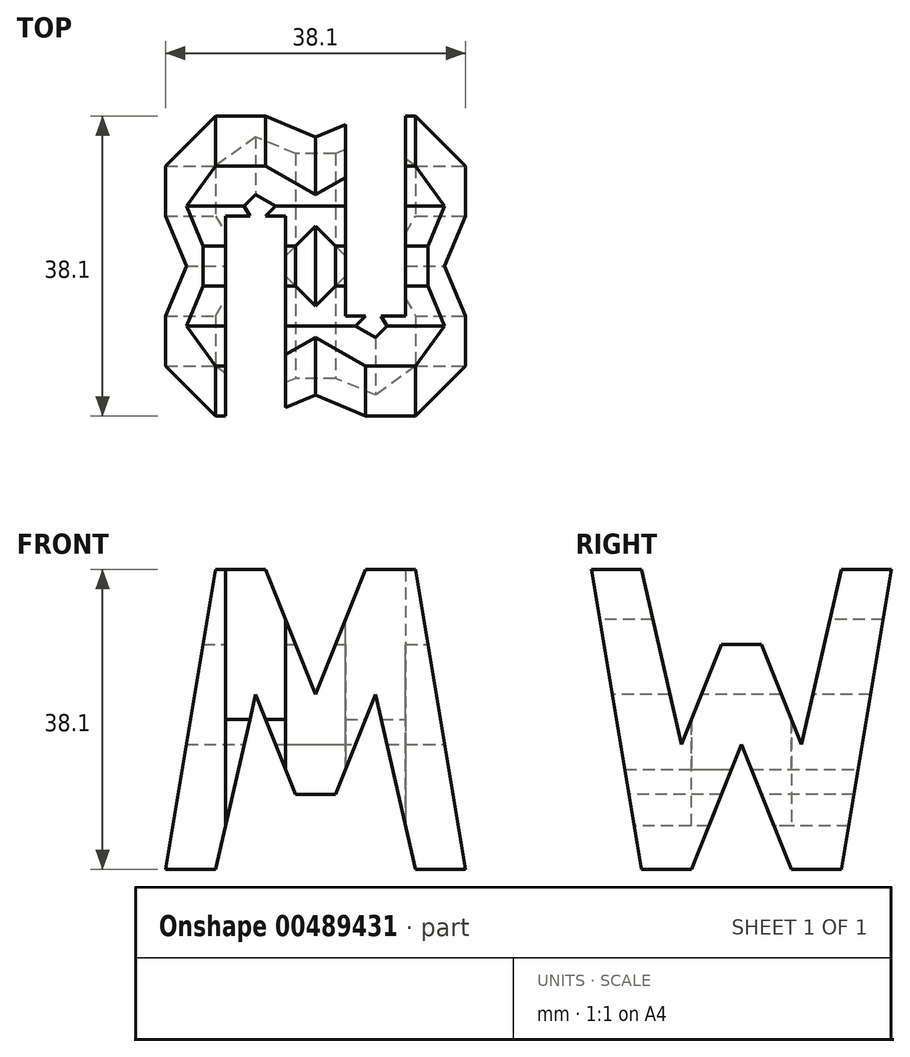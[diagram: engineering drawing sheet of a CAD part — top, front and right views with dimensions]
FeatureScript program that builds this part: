
annotation { "Feature Type Name" : "Feature", "Feature Type Description" : "" }
export const myFeature = defineFeature(function(context is Context, id is Id, definition is map)
    precondition{}
    {
        {
            var Q0;
            Q0=qCreatedBy(makeId("Front.planeOp"),FACE);
            var sketch = newSketch(context, id + "F0", { "sketchPlane" : qUnion([Q0])});
            skLineSegment(sketch, "E0.bottom", {"start": v(0, 0) * mm, "end": v(38.1, 0) * mm});
            skLineSegment(sketch, "E0.top", {"start": v(0, 38.1) * mm, "end": v(38.1, 38.1) * mm});
            skLineSegment(sketch, "E0.left", {"start": v(0, 0) * mm, "end": v(0, 38.1) * mm});
            skLineSegment(sketch, "E0.right", {"start": v(38.1, 0) * mm, "end": v(38.1, 38.1) * mm});
            skSolve(sketch);
        }
        {
            var Q0;
            Q0 = qSketchRegion(id + "F0", true);
            extrude(context, id + "F1", {"entities" : qUnion([Q0]), "depth" : 38.1 * mm, "offsetDistance" : 25.4 * mm});
        }
        {
            var Q0;
            Q0=qCreatedBy(makeId("Front.planeOp"),FACE);
            cPlane(context, id + "F2", {"entities" : qUnion([Q0]), "cplaneType" : CPlaneType.OFFSET, "offset" : 38.1 * mm, "width" : 152.4 * mm, "height" : 152.4 * mm});
        }
        {
            var Q0;
            Q0=qCreatedBy(makeId("Right.planeOp"),FACE);
            cPlane(context, id + "F3", {"entities" : qUnion([Q0]), "cplaneType" : CPlaneType.OFFSET, "offset" : 38.1 * mm, "width" : 152.4 * mm, "height" : 152.4 * mm});
        }
        {
            var Q0;
            Q0=qCreatedBy(id+"F3.planeOp",FACE);
            var sketch = newSketch(context, id + "F4", { "sketchPlane" : qUnion([Q0])});
            skLineSegment(sketch, "E1.bottom", {"start": v(0, 0) * mm, "end": v(-38.1, 0) * mm});
            skLineSegment(sketch, "E1.top", {"start": v(0, 38.1) * mm, "end": v(-38.1, 38.1) * mm});
            skLineSegment(sketch, "E1.left", {"start": v(0, 0) * mm, "end": v(0, 38.1) * mm});
            skLineSegment(sketch, "E1.right", {"start": v(-38.1, 0) * mm, "end": v(-38.1, 38.1) * mm});
            skLineSegment(sketch, "E2", {"start": v(0, 38.1) * mm, "end": v(-6.35, 0) * mm});
            skLineSegment(sketch, "E3", {"start": v(-38.1, 38.1) * mm, "end": v(-31.75, 0) * mm});
            skLineSegment(sketch, "E4", {"start": v(-25.4, 0) * mm, "end": v(-19.05, 15.88) * mm});
            skLineSegment(sketch, "E5", {"start": v(-12.7, 0) * mm, "end": v(-19.05, 15.88) * mm});
            skLineSegment(sketch, "E6", {"start": v(-31.75, 38.1) * mm, "end": v(-26.67, 15.88) * mm});
            skLineSegment(sketch, "E7", {"start": v(-6.35, 38.1) * mm, "end": v(-11.43, 15.88) * mm});
            skLineSegment(sketch, "E8", {"start": v(-11.43, 15.88) * mm, "end": v(-16.5, 28.58) * mm});
            skLineSegment(sketch, "E9", {"start": v(-26.67, 15.88) * mm, "end": v(-21.59, 28.58) * mm});
            skLineSegment(sketch, "E10", {"start": v(-16.5, 28.58) * mm, "end": v(-21.59, 28.58) * mm});
            skLineSegment(sketch, "E11", {"start": v(-38.1, 0) * mm, "end": v(0, 0) * mm});
            skSolve(sketch);
        }
        {
            var Q0;
            {var subQ1=sQuery(id+"F4.wireOp",EDGE,"E6");Q0=makeQuery(id+"F4.imprint","IMPRINT",FACE,{"disambiguationData":[TD([[makeQuery(id+"F4.imprint","IMPRINT",EDGE,{"derivedFrom":subQ1}),1.0]])]});}
            var Q1;
            {var subQ0=sQuery(id+"F4.wireOp",EDGE,"E1.right");Q1=makeQuery(id+"F4.imprint","IMPRINT",FACE,{"disambiguationData":[TD([[makeQuery(id+"F4.imprint","IMPRINT",EDGE,{"derivedFrom":subQ0}),-1.0]])]});}
            var Q2;
            {var subQ0=sQuery(id+"F4.wireOp",EDGE,"E4");Q2=makeQuery(id+"F4.imprint","IMPRINT",FACE,{"disambiguationData":[TD([[makeQuery(id+"F4.imprint","IMPRINT",EDGE,{"derivedFrom":subQ0}),-1.0]])]});}
            var Q3;
            {var subQ0=sQuery(id+"F4.wireOp",EDGE,"E1.left");Q3=makeQuery(id+"F4.imprint","IMPRINT",FACE,{"disambiguationData":[TD([[makeQuery(id+"F4.imprint","IMPRINT",EDGE,{"derivedFrom":subQ0}),1.0]])]});}
            extrude(context, id + "F5", {"entities" : qUnion([Q0, Q1, Q2, Q3]), "operationType" : NewBodyOperationType.REMOVE, "oppositeDirection" : true, "depth" : 38.1 * mm, "offsetDistance" : 25.4 * mm});
        }
        {
            var Q0;
            Q0=qCreatedBy(id+"F2.planeOp",FACE);
            var sketch = newSketch(context, id + "F6", { "sketchPlane" : qUnion([Q0])});
            skLineSegment(sketch, "E12", {"start": v(0, 38.1) * mm, "end": v(0, 0) * mm});
            skLineSegment(sketch, "E13", {"start": v(38.1, 0) * mm, "end": v(0, 0) * mm});
            skLineSegment(sketch, "E14", {"start": v(38.1, 0) * mm, "end": v(38.1, 38.1) * mm});
            skLineSegment(sketch, "E15", {"start": v(38.1, 38.1) * mm, "end": v(0, 38.1) * mm});
            skLineSegment(sketch, "E16", {"start": v(0, 0) * mm, "end": v(6.35, 38.1) * mm});
            skLineSegment(sketch, "E17", {"start": v(12.7, 38.1) * mm, "end": v(19.05, 22.23) * mm});
            skLineSegment(sketch, "E18", {"start": v(19.05, 22.23) * mm, "end": v(25.4, 38.1) * mm});
            skLineSegment(sketch, "E19", {"start": v(31.75, 38.1) * mm, "end": v(38.1, 0) * mm});
            skLineSegment(sketch, "E20", {"start": v(31.75, 0) * mm, "end": v(26.67, 22.23) * mm});
            skLineSegment(sketch, "E21", {"start": v(26.67, 22.22) * mm, "end": v(21.59, 9.53) * mm});
            skLineSegment(sketch, "E22", {"start": v(21.59, 9.53) * mm, "end": v(16.5, 9.53) * mm});
            skLineSegment(sketch, "E23", {"start": v(16.5, 9.53) * mm, "end": v(11.43, 22.23) * mm});
            skLineSegment(sketch, "E24", {"start": v(11.43, 22.23) * mm, "end": v(6.35, 0) * mm});
            skSolve(sketch);
        }
        {
            var Q0;
            {var subQ0=sQuery(id+"F6.wireOp",EDGE,"E12");Q0=makeQuery(id+"F6.imprint","IMPRINT",FACE,{"disambiguationData":[TD([[makeQuery(id+"F6.imprint","IMPRINT",EDGE,{"derivedFrom":subQ0}),1.0]])]});}
            var Q1;
            {var subQ0=sQuery(id+"F6.wireOp",EDGE,"E17");Q1=makeQuery(id+"F6.imprint","IMPRINT",FACE,{"disambiguationData":[TD([[makeQuery(id+"F6.imprint","IMPRINT",EDGE,{"derivedFrom":subQ0}),1.0]])]});}
            var Q2;
            {var subQ0=sQuery(id+"F6.wireOp",EDGE,"E14");Q2=makeQuery(id+"F6.imprint","IMPRINT",FACE,{"disambiguationData":[TD([[makeQuery(id+"F6.imprint","IMPRINT",EDGE,{"derivedFrom":subQ0}),1.0]])]});}
            var Q3;
            {var subQ0=sQuery(id+"F6.wireOp",EDGE,"E20");Q3=makeQuery(id+"F6.imprint","IMPRINT",FACE,{"disambiguationData":[TD([[makeQuery(id+"F6.imprint","IMPRINT",EDGE,{"derivedFrom":subQ0}),1.0]])]});}
            extrude(context, id + "F7", {"entities" : qUnion([Q0, Q1, Q2, Q3]), "operationType" : NewBodyOperationType.REMOVE, "oppositeDirection" : true, "depth" : 38.1 * mm, "offsetDistance" : 25.4 * mm});
        }
        {
            var Q0;
            Q0=qCreatedBy(makeId("Top.planeOp"),FACE);
            var sketch = newSketch(context, id + "F8", { "sketchPlane" : qUnion([Q0])});
            skLineSegment(sketch, "E25", {"start": v(7.62, -38.1) * mm, "end": v(7.62, -12.7) * mm});
            skLineSegment(sketch, "E26", {"start": v(7.62, -12.7) * mm, "end": v(15.24, -12.7) * mm});
            skLineSegment(sketch, "E27", {"start": v(15.24, -12.7) * mm, "end": v(15.24, -38.1) * mm});
            skLineSegment(sketch, "E28", {"start": v(22.86, 0) * mm, "end": v(22.86, -25.4) * mm});
            skLineSegment(sketch, "E29", {"start": v(22.86, -25.4) * mm, "end": v(30.48, -25.4) * mm});
            skLineSegment(sketch, "E30", {"start": v(30.48, -25.4) * mm, "end": v(30.48, 0) * mm});
            skLineSegment(sketch, "E31", {"start": v(0, 0) * mm, "end": v(0, -38.1) * mm});
            skLineSegment(sketch, "E32", {"start": v(0, -38.1) * mm, "end": v(38.1, -38.1) * mm});
            skLineSegment(sketch, "E33", {"start": v(0, 0) * mm, "end": v(38.1, 0) * mm});
            skLineSegment(sketch, "E34", {"start": v(38.1, 0) * mm, "end": v(38.1, -38.1) * mm});
            skSolve(sketch);
        }
        {
            var Q0;
            {var subQ0=sQuery(id+"F8.wireOp",EDGE,"E25");Q0=makeQuery(id+"F8.imprint","IMPRINT",FACE,{"disambiguationData":[TD([[makeQuery(id+"F8.imprint","IMPRINT",EDGE,{"derivedFrom":subQ0}),-1.0]])]});}
            var Q1;
            {var subQ0=sQuery(id+"F8.wireOp",EDGE,"E28");Q1=makeQuery(id+"F8.imprint","IMPRINT",FACE,{"disambiguationData":[TD([[makeQuery(id+"F8.imprint","IMPRINT",EDGE,{"derivedFrom":subQ0}),1.0]])]});}
            extrude(context, id + "F9", {"entities" : qUnion([Q0, Q1]), "operationType" : NewBodyOperationType.REMOVE, "depth" : 38.1 * mm, "offsetDistance" : 25.4 * mm});
        }
    });
